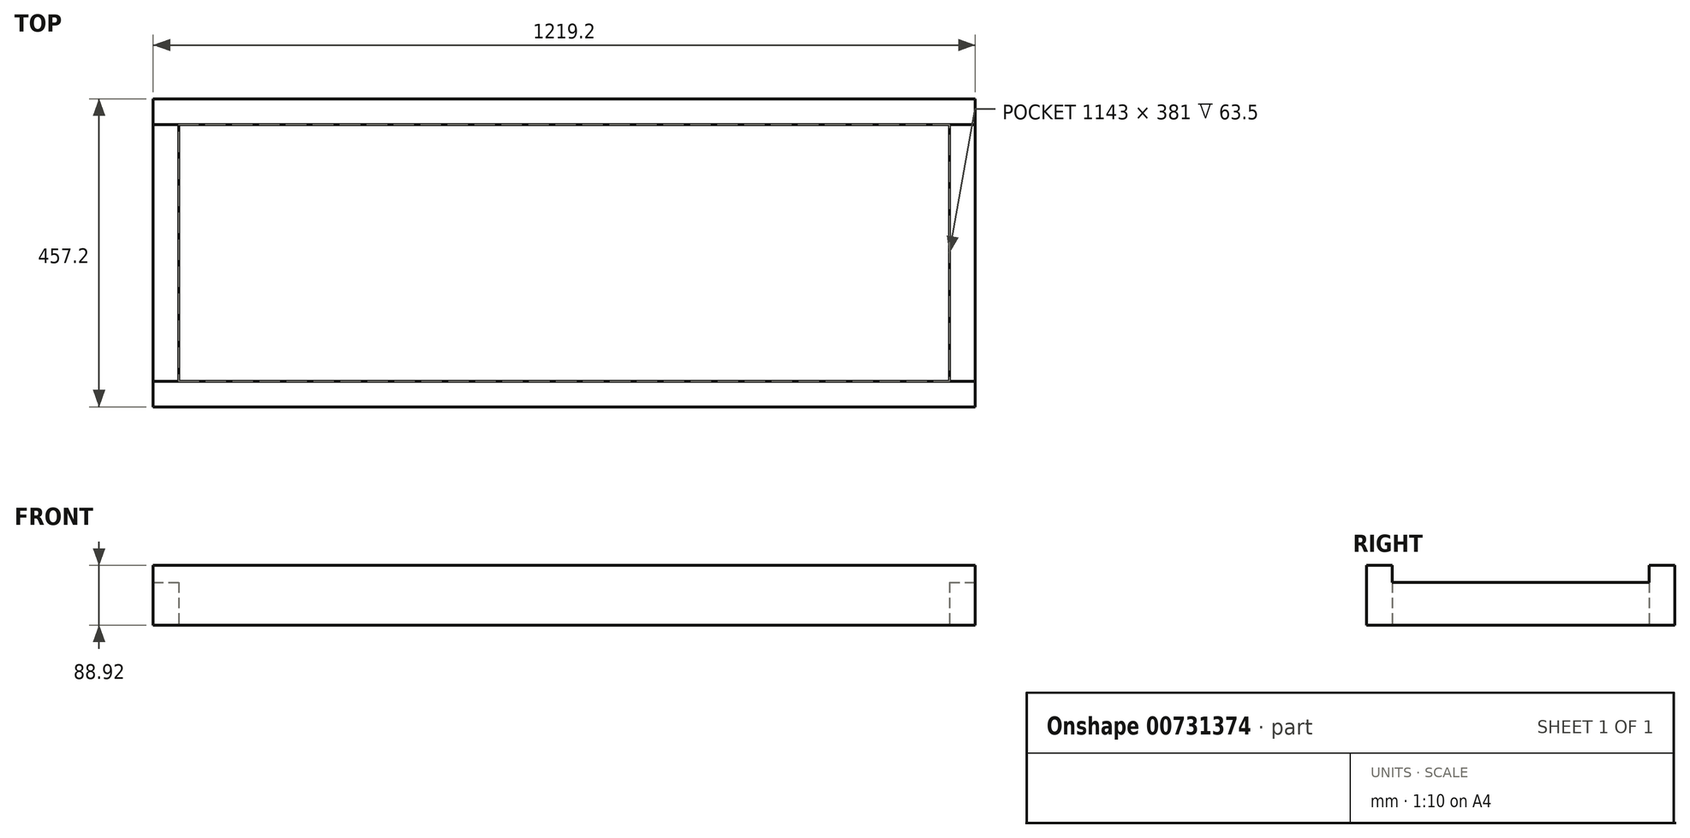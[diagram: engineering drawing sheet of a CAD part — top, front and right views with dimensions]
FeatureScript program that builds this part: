
annotation { "Feature Type Name" : "Feature", "Feature Type Description" : "" }
export const myFeature = defineFeature(function(context is Context, id is Id, definition is map)
    precondition{}
    {
        {
            var Q0;
            Q0=qCreatedBy(makeId("Top.planeOp"),FACE);
            var sketch = newSketch(context, id + "F0", { "sketchPlane" : qUnion([Q0])});
            skLineSegment(sketch, "E0.bottom", {"start": v(-609.6, 228.6) * mm, "end": v(609.6, 228.6) * mm});
            skLineSegment(sketch, "E0.top", {"start": v(-609.6, -228.6) * mm, "end": v(609.6, -228.6) * mm});
            skLineSegment(sketch, "E0.left", {"start": v(-609.6, 228.6) * mm, "end": v(-609.6, -228.6) * mm});
            skLineSegment(sketch, "E0.right", {"start": v(609.6, 228.6) * mm, "end": v(609.6, -228.6) * mm});
            skPoint(sketch, "E0.middle", {"position": v(0, 0) * mm});
            skSolve(sketch);
        }
        {
            var Q0;
            Q0 = qSketchRegion(id + "F0", true);
            extrude(context, id + "F1", {"entities" : qUnion([Q0]), "depth" : 1 / 50.8 * mm, "offsetDistance" : 25.4 * mm});
        }
        {
            var Q0;
            Q0=makeQuery(id+"F1.opExtrude","CAP_FACE",FACE,{"disambiguationData":[OSD([sQuery(id+"F0.wireOp",EDGE,"E0.bottom"),sQuery(id+"F0.wireOp",EDGE,"E0.top"),sQuery(id+"F0.wireOp",EDGE,"E0.left"),sQuery(id+"F0.wireOp",EDGE,"E0.right")])],"isStart":false});
            var sketch = newSketch(context, id + "F2", { "sketchPlane" : qUnion([Q0])});
            skLineSegment(sketch, "E1.bottom", {"start": v(-609.6, -228.6) * mm, "end": v(609.6, -228.6) * mm});
            skLineSegment(sketch, "E1.top", {"start": v(-609.6, -190.5) * mm, "end": v(609.6, -190.5) * mm});
            skLineSegment(sketch, "E1.left", {"start": v(-609.6, -228.6) * mm, "end": v(-609.6, -190.5) * mm});
            skLineSegment(sketch, "E1.right", {"start": v(609.6, -228.6) * mm, "end": v(609.6, -190.5) * mm});
            skLineSegment(sketch, "E2.MirrorCS", {"start": v(-609.6, 190.5) * mm, "end": v(609.6, 190.5) * mm});
            skLineSegment(sketch, "E3.MirrorCS", {"start": v(-609.6, 228.6) * mm, "end": v(-609.6, 190.5) * mm});
            skLineSegment(sketch, "E4.MirrorCS", {"start": v(-609.6, 228.6) * mm, "end": v(609.6, 228.6) * mm});
            skLineSegment(sketch, "E5.MirrorCS", {"start": v(609.6, 228.6) * mm, "end": v(609.6, 190.5) * mm});
            skSolve(sketch);
        }
        {
            var Q0;
            Q0 = qSketchRegion(id + "F2", true);
            extrude(context, id + "F3", {"entities" : qUnion([Q0]), "operationType" : NewBodyOperationType.ADD, "depth" : 88.9 * mm, "offsetDistance" : 25.4 * mm});
        }
        {
            var Q0;
            Q0=makeQuery(id+"F1.opExtrude","CAP_FACE",FACE,{"disambiguationData":[OSD([sQuery(id+"F0.wireOp",EDGE,"E0.bottom"),sQuery(id+"F0.wireOp",EDGE,"E0.top"),sQuery(id+"F0.wireOp",EDGE,"E0.left"),sQuery(id+"F0.wireOp",EDGE,"E0.right")])],"isStart":false});
            var sketch = newSketch(context, id + "F4", { "sketchPlane" : qUnion([Q0])});
            skLineSegment(sketch, "E6.bottom", {"start": v(-609.6, 190.5) * mm, "end": v(-571.5, 190.5) * mm});
            skLineSegment(sketch, "E6.top", {"start": v(-609.6, -190.5) * mm, "end": v(-571.5, -190.5) * mm});
            skLineSegment(sketch, "E6.left", {"start": v(-609.6, 190.5) * mm, "end": v(-609.6, -190.5) * mm});
            skLineSegment(sketch, "E6.right", {"start": v(-571.5, 190.5) * mm, "end": v(-571.5, -190.5) * mm});
            skLineSegment(sketch, "E7.MirrorCS", {"start": v(609.6, 190.5) * mm, "end": v(571.5, 190.5) * mm});
            skLineSegment(sketch, "E8.MirrorCS", {"start": v(571.5, 190.5) * mm, "end": v(571.5, -190.5) * mm});
            skLineSegment(sketch, "E9.MirrorCS", {"start": v(609.6, -190.5) * mm, "end": v(571.5, -190.5) * mm});
            skLineSegment(sketch, "E10.MirrorCS", {"start": v(609.6, 190.5) * mm, "end": v(609.6, -190.5) * mm});
            skSolve(sketch);
        }
        {
            var Q0;
            Q0 = qSketchRegion(id + "F4", true);
            extrude(context, id + "F5", {"entities" : qUnion([Q0]), "operationType" : NewBodyOperationType.ADD, "depth" : 63.5 * mm, "offsetDistance" : 25.4 * mm});
        }
    });
